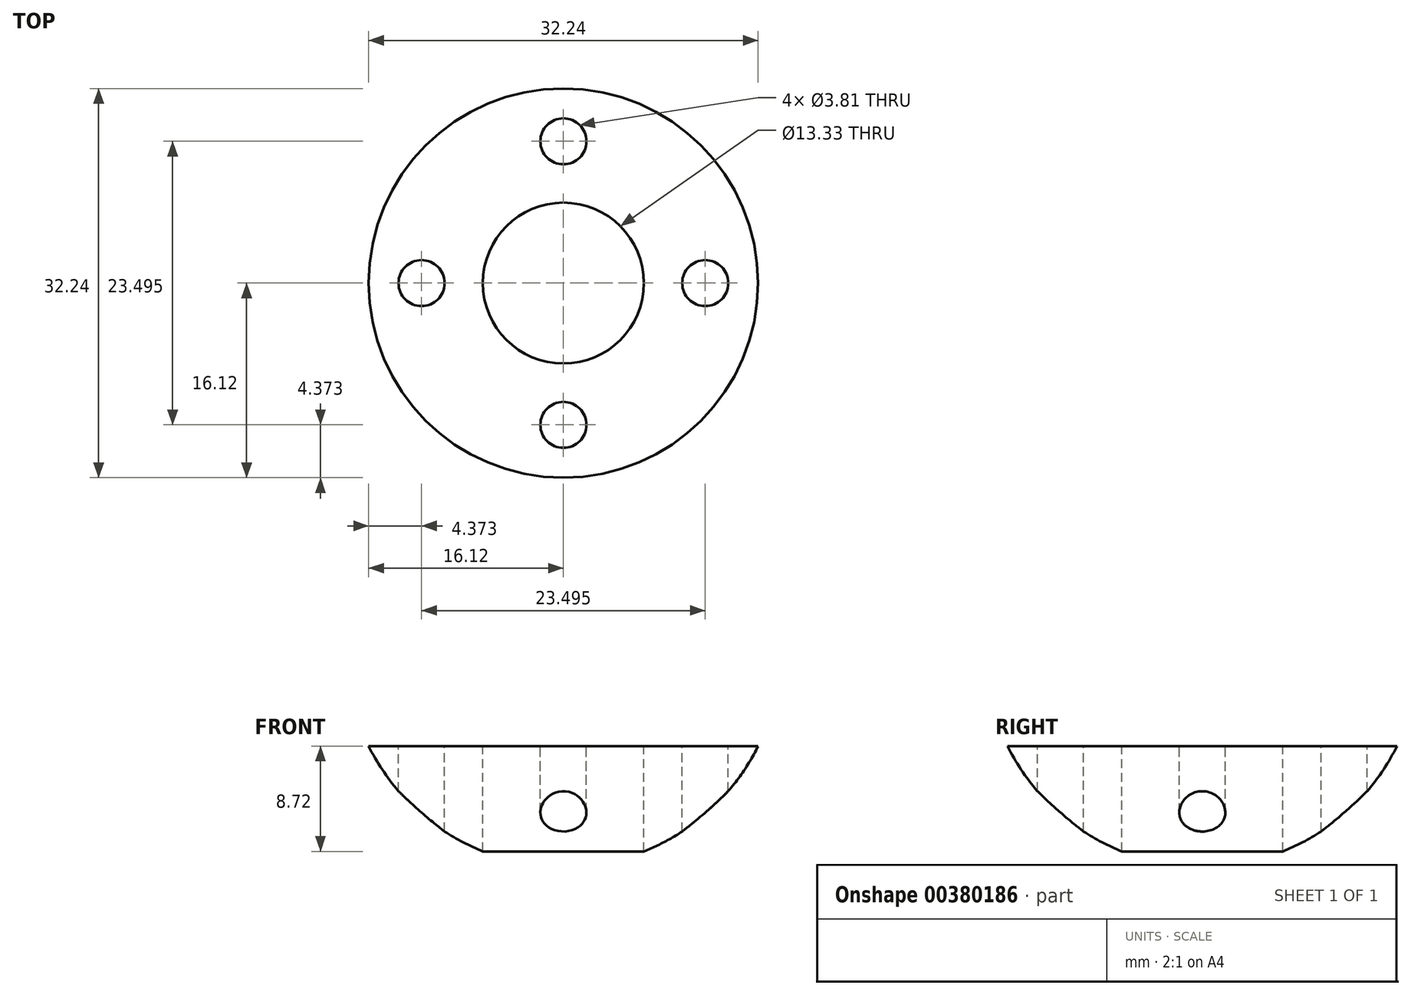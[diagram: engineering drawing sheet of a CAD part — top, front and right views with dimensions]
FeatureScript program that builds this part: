
annotation { "Feature Type Name" : "Feature", "Feature Type Description" : "" }
export const myFeature = defineFeature(function(context is Context, id is Id, definition is map)
    precondition{}
    {
        {
            var Q0;
            Q0=qCreatedBy(makeId("Front.planeOp"),FACE);
            var sketch = newSketch(context, id + "F0", { "sketchPlane" : qUnion([Q0])});
            skArc(sketch, "E0", {"start": v(0, -18) * mm, "mid": v(18, 0) * mm, "end": v(0, 18) * mm});
            skLineSegment(sketch, "E1", {"start": v(0, 18) * mm, "end": v(0, -18) * mm, "construction": true});
            skLineSegment(sketch, "E2", {"start": v(0, 18) * mm, "end": v(0, -18) * mm});
            skSolve(sketch);
        }
        {
            var Q0;
            Q0=makeQuery(id+"F0.imprint","IMPRINT",FACE,{"disambiguationData":[TD([[makeQuery(id+"F0.imprint","IMPRINT",EDGE,{"derivedFrom":sQuery(id+"F0.wireOp",EDGE,"E0")}),1.0]])]});
            var Q1;
            Q1=sQuery(id+"F0.wireOp",EDGE,"E2");
            revolve(context, id + "F1", {"surfaceOperationType" : NewSurfaceOperationType.NEW, "entities" : qUnion([Q0]), "axis" : qUnion([Q1]), "revolveType" : RevolveType.FULL});
        }
        {
            var Q0;
            Q0=qCreatedBy(makeId("Right.planeOp"),FACE);
            var sketch = newSketch(context, id + "F2", { "sketchPlane" : qUnion([Q0])});
            skArc(sketch, "E3", {"start": v(16.12, -8) * mm, "mid": v(0, 18) * mm, "end": v(-16.12, -8) * mm});
            skLineSegment(sketch, "E4", {"start": v(16.12, -8) * mm, "end": v(-16.12, -8) * mm});
            skSolve(sketch);
        }
        {
            var Q0;
            Q0 = qSketchRegion(id + "F2", true);
            extrude(context, id + "F3", {"entities" : qUnion([Q0]), "operationType" : NewBodyOperationType.REMOVE, "endBound" : BoundingType.SYMMETRIC, "oppositeDirection" : true, "depth" : 36 * mm});
        }
        {
            var Q0;
            Q0=makeQuery(id+"F3.boolean.opBoolean","COPY",FACE,{"derivedFrom":makeQuery(id+"F3.opExtrude","SWEPT_FACE",FACE,{"disambiguationData":[OSD([sQuery(id+"F2.wireOp",EDGE,"E4")])]})});
            var sketch = newSketch(context, id + "F4", { "sketchPlane" : qUnion([Q0])});
            skCircle(sketch, "E5", {"center": v(0, 0) * mm, "radius": 6.67 * mm});
            skCircle(sketch, "E6", {"center": v(0, 0) * mm, "radius": 11.75 * mm, "construction": true});
            skLineSegment(sketch, "E7", {"start": v(0, 0) * mm, "end": v(0, 12.88) * mm, "construction": true});
            skLineSegment(sketch, "E8", {"start": v(0, 0) * mm, "end": v(11.48, 0) * mm, "construction": true});
            skLineSegment(sketch, "E9", {"start": v(0, 0) * mm, "end": v(0, -11.5) * mm, "construction": true});
            skLineSegment(sketch, "E10", {"start": v(0.16, 0) * mm, "end": v(-13.02, 0) * mm, "construction": true});
            skCircle(sketch, "E11", {"center": v(-11.75, 0) * mm, "radius": 1.9 * mm});
            skCircle(sketch, "E12", {"center": v(11.75, 0) * mm, "radius": 1.9 * mm});
            skCircle(sketch, "E13", {"center": v(0, -11.75) * mm, "radius": 1.9 * mm});
            skCircle(sketch, "E14", {"center": v(0, 11.75) * mm, "radius": 1.9 * mm});
            skSolve(sketch);
        }
        {
            var Q0;
            Q0=makeQuery(id+"F4.imprint","IMPRINT",FACE,{"disambiguationData":[TD([[makeQuery(id+"F4.imprint","IMPRINT",EDGE,{"derivedFrom":sQuery(id+"F4.wireOp",EDGE,"E13")}),1.0]])]});
            var Q1;
            Q1=makeQuery(id+"F4.imprint","IMPRINT",FACE,{"disambiguationData":[TD([[makeQuery(id+"F4.imprint","IMPRINT",EDGE,{"derivedFrom":sQuery(id+"F4.wireOp",EDGE,"E12")}),1.0]])]});
            var Q2;
            Q2=makeQuery(id+"F4.imprint","IMPRINT",FACE,{"disambiguationData":[TD([[makeQuery(id+"F4.imprint","IMPRINT",EDGE,{"derivedFrom":sQuery(id+"F4.wireOp",EDGE,"E14")}),1.0]])]});
            var Q3;
            Q3=makeQuery(id+"F4.imprint","IMPRINT",FACE,{"disambiguationData":[TD([[makeQuery(id+"F4.imprint","IMPRINT",EDGE,{"derivedFrom":sQuery(id+"F4.wireOp",EDGE,"E11")}),1.0]])]});
            var Q4;
            Q4=makeQuery(id+"F4.imprint","IMPRINT",FACE,{"disambiguationData":[TD([[makeQuery(id+"F4.imprint","IMPRINT",EDGE,{"derivedFrom":sQuery(id+"F4.wireOp",EDGE,"854632fd-7fc5-4a25-a73e-f75494d8c970")}),1.0]])]});
            var Q5;
            Q5=makeQuery(id+"F4.imprint","IMPRINT",FACE,{"disambiguationData":[TD([[makeQuery(id+"F4.imprint","IMPRINT",EDGE,{"derivedFrom":sQuery(id+"F4.wireOp",EDGE,"E5")}),1.0]])]});
            extrude(context, id + "F5", {"entities" : qUnion([Q0, Q1, Q2, Q3, Q4, Q5]), "operationType" : NewBodyOperationType.REMOVE, "endBound" : BoundingType.UP_TO_NEXT, "oppositeDirection" : true, "depth" : 25.4 * mm});
        }
    });
